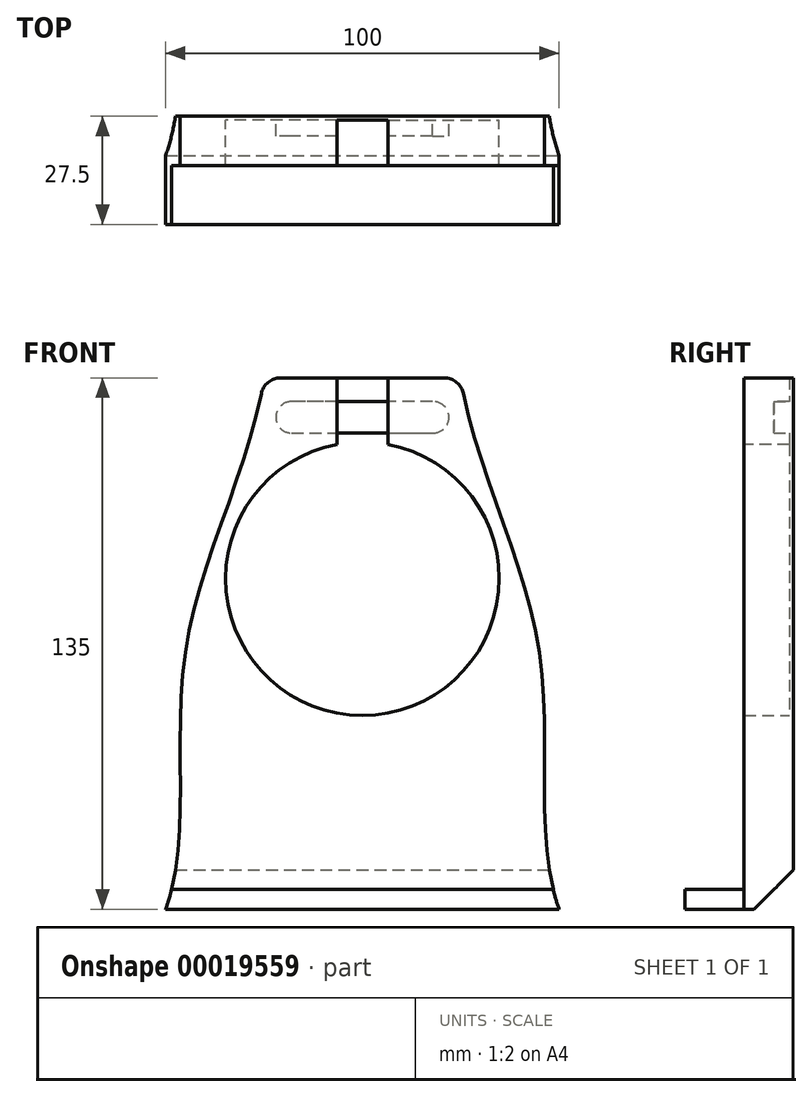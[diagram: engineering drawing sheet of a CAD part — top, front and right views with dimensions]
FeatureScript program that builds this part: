
annotation { "Feature Type Name" : "Feature", "Feature Type Description" : "" }
export const myFeature = defineFeature(function(context is Context, id is Id, definition is map)
    precondition{}
    {
        {
            var Q0;
            Q0=qCreatedBy(makeId("Front.planeOp"),FACE);
            var sketch = newSketch(context, id + "F0", { "sketchPlane" : qUnion([Q0])});
            skCircle(sketch, "E0", {"center": v(0, 84) * mm, "radius": 34.75 * mm});
            skLineSegment(sketch, "E1", {"start": v(-50, 0) * mm, "end": v(0, 0) * mm});
            skLineSegment(sketch, "E2", {"start": v(-20.79, 135) * mm, "end": v(0, 135) * mm});
            skFitSpline(sketch, "E3", {"points": [v(-50, 0) * mm, v(-45, 65.07) * mm, v(-24.94, 135) * mm], "startDerivative": vector(40.67, 111.81) * mm, "endDerivative": vector(23.97, 143.13) * mm});
            skLineSegment(sketch, "E4", {"start": v(0, 144.2) * mm, "end": v(0, -28.62) * mm, "construction": true});
            skLineSegment(sketch, "E5.MirrorCS", {"start": v(20.79, 135) * mm, "end": v(0, 135) * mm});
            skFitSpline(sketch, "E6.MirrorCS", {"points": [v(50, 0) * mm, v(45, 65.07) * mm, v(24.94, 135) * mm], "startDerivative": vector(-40.67, 111.81) * mm, "endDerivative": vector(-23.97, 143.13) * mm});
            skLineSegment(sketch, "E7.MirrorCS", {"start": v(50, 0) * mm, "end": v(0, 0) * mm});
            skArc(sketch, "E8.filletArc", {"start": v(-20.79, 135) * mm, "mid": v(-23.95, 133.87) * mm, "end": v(-25.69, 131) * mm});
            skArc(sketch, "E9.filletArc", {"start": v(25.69, 131) * mm, "mid": v(23.95, 133.87) * mm, "end": v(20.79, 135) * mm});
            skSolve(sketch);
        }
        {
            var Q0;
            Q0=makeQuery(id+"F0.imprint","IMPRINT",FACE,{"disambiguationData":[TD([[makeQuery(id+"F0.imprint","IMPRINT",EDGE,{"derivedFrom":sQuery(id+"F0.wireOp",EDGE,"E0")}),1.0]])]});
            extrude(context, id + "F1", {"entities" : qUnion([Q0]), "offsetDistance" : 25 * mm, "depth" : 1 * mm});
        }
        {
            var Q0;
            Q0 = qSketchRegion(id + "F0", true);
            extrude(context, id + "F2", {"entities" : qUnion([Q0]), "operationType" : NewBodyOperationType.ADD, "offsetDistance" : 25 * mm, "depth" : 12.5 * mm});
        }
        {
            var Q0;
            Q0=makeQuery(id+"F2.opExtrude","CAP_FACE",FACE,{"disambiguationData":[OSD([sQuery(id+"F0.wireOp",EDGE,"E0"),sQuery(id+"F0.wireOp",EDGE,"E1"),sQuery(id+"F0.wireOp",EDGE,"E2"),sQuery(id+"F0.wireOp",EDGE,"E3"),sQuery(id+"F0.wireOp",EDGE,"E5.MirrorCS"),sQuery(id+"F0.wireOp",EDGE,"E6.MirrorCS"),sQuery(id+"F0.wireOp",EDGE,"E7.MirrorCS"),sQuery(id+"F0.wireOp",EDGE,"E8.filletArc"),sQuery(id+"F0.wireOp",EDGE,"E9.filletArc")])],"isStart":false});
            var sketch = newSketch(context, id + "F3", { "sketchPlane" : qUnion([Q0])});
            skLineSegment(sketch, "E10", {"start": v(-48.5, 5) * mm, "end": v(48.5, 5) * mm});
            skLineSegment(sketch, "E11", {"start": v(-50, 0) * mm, "end": v(50, 0) * mm});
            skArc(sketch, "E12", {"start": v(-50, 0) * mm, "mid": v(-49.18, 2.48) * mm, "end": v(-48.5, 5) * mm});
            skArc(sketch, "E13", {"start": v(48.5, 5) * mm, "mid": v(49.17, 2.48) * mm, "end": v(50, 0) * mm});
            skSolve(sketch);
        }
        {
            var Q0;
            Q0 = qSketchRegion(id + "F3", true);
            extrude(context, id + "F4", {"entities" : qUnion([Q0]), "operationType" : NewBodyOperationType.ADD, "depth" : 15 * mm});
        }
        {
            var Q0;
            {var subQ0=sQuery(id+"F0.wireOp",EDGE,"E0");var subQ1=sQuery(id+"F0.wireOp",EDGE,"E2");var subQ2=sQuery(id+"F0.wireOp",EDGE,"E3");var subQ3=sQuery(id+"F0.wireOp",EDGE,"E5.MirrorCS");var subQ4=sQuery(id+"F0.wireOp",EDGE,"E6.MirrorCS");var subQ5=sQuery(id+"F0.wireOp",EDGE,"E8.filletArc");var subQ6=sQuery(id+"F0.wireOp",EDGE,"E9.filletArc");var subQ7=makeQuery(id+"F2.opExtrude","CAP_FACE",FACE,{"disambiguationData":[OSD([subQ0,sQuery(id+"F0.wireOp",EDGE,"E1"),subQ1,subQ2,subQ3,subQ4,sQuery(id+"F0.wireOp",EDGE,"E7.MirrorCS"),subQ5,subQ6])],"isStart":false});Q0=makeQuery(id+"F4.boolean.opBoolean","SPLIT",FACE,{"disambiguationData":[TD([makeQuery(id+"F2.opExtrude","SWEPT_FACE",FACE,{"disambiguationData":[OSD([subQ0])]})])],"derivedFrom":subQ7});}
            var sketch = newSketch(context, id + "F5", { "sketchPlane" : qUnion([Q0])});
            skLineSegment(sketch, "E14", {"start": v(-6.5, 135) * mm, "end": v(6.5, 135) * mm});
            skLineSegment(sketch, "E15", {"start": v(0, 114.05) * mm, "end": v(0, 95.22) * mm, "construction": true});
            skLineSegment(sketch, "E16", {"start": v(-6.5, 135) * mm, "end": v(-6.5, 118.14) * mm});
            skLineSegment(sketch, "E17", {"start": v(6.5, 135) * mm, "end": v(6.5, 118.14) * mm});
            skArc(sketch, "E18", {"start": v(6.5, 118.14) * mm, "mid": v(0, 118.75) * mm, "end": v(-6.5, 118.14) * mm});
            skSolve(sketch);
        }
        {
            var Q0;
            Q0 = qSketchRegion(id + "F5", true);
            extrude(context, id + "F6", {"entities" : qUnion([Q0]), "operationType" : NewBodyOperationType.REMOVE, "oppositeDirection" : true, "depth" : 11.5 * mm});
        }
        {
            var Q0;
            {var subQ0=sQuery(id+"F0.wireOp",EDGE,"E0");Q0=makeQuery(id+"F2.boolean.opBoolean","MERGE",FACE,{"derivedFrom":[makeQuery(id+"F1.opExtrude","CAP_FACE",FACE,{"disambiguationData":[OSD([subQ0])],"isStart":true}),makeQuery(id+"F2.opExtrude","CAP_FACE",FACE,{"disambiguationData":[OSD([subQ0,sQuery(id+"F0.wireOp",EDGE,"E1"),sQuery(id+"F0.wireOp",EDGE,"E2"),sQuery(id+"F0.wireOp",EDGE,"E3"),sQuery(id+"F0.wireOp",EDGE,"E5.MirrorCS"),sQuery(id+"F0.wireOp",EDGE,"E6.MirrorCS"),sQuery(id+"F0.wireOp",EDGE,"E7.MirrorCS"),sQuery(id+"F0.wireOp",EDGE,"E8.filletArc"),sQuery(id+"F0.wireOp",EDGE,"E9.filletArc")])],"isStart":true})]});}
            var sketch = newSketch(context, id + "F7", { "sketchPlane" : qUnion([Q0])});
            skArc(sketch, "E19", {"start": v(-17.77, 129) * mm, "mid": v(-22, 125) * mm, "end": v(-17.77, 121) * mm});
            skArc(sketch, "E20", {"start": v(18, 121) * mm, "mid": v(22, 125) * mm, "end": v(18, 129) * mm});
            skLineSegment(sketch, "E21", {"start": v(0, 111.96) * mm, "end": v(0, 95.55) * mm, "construction": true});
            skLineSegment(sketch, "E22", {"start": v(-18, 125) * mm, "end": v(18, 125) * mm, "construction": true});
            skLineSegment(sketch, "E23", {"start": v(-17.77, 129) * mm, "end": v(18, 129) * mm});
            skLineSegment(sketch, "E24", {"start": v(18, 121) * mm, "end": v(-17.77, 121) * mm});
            skSolve(sketch);
        }
        {
            var Q0;
            Q0 = qSketchRegion(id + "F7", true);
            extrude(context, id + "F8", {"entities" : qUnion([Q0]), "operationType" : NewBodyOperationType.REMOVE, "oppositeDirection" : true, "offsetDistance" : 25 * mm, "depth" : 5 * mm});
        }
        {
            var Q0;
            Q0=qCreatedBy(makeId("Right.planeOp"),FACE);
            var sketch = newSketch(context, id + "F9", { "sketchPlane" : qUnion([Q0])});
            skLineSegment(sketch, "E25", {"start": v(0, 0) * mm, "end": v(0, 10) * mm});
            skLineSegment(sketch, "E26", {"start": v(0, 10) * mm, "end": v(-10, 0) * mm});
            skLineSegment(sketch, "E27", {"start": v(-10, 0) * mm, "end": v(0, 0) * mm});
            skSolve(sketch);
        }
        {
            var Q0;
            Q0 = qSketchRegion(id + "F9", true);
            extrude(context, id + "F10", {"entities" : qUnion([Q0]), "operationType" : NewBodyOperationType.REMOVE, "endBound" : BoundingType.THROUGH_ALL, "oppositeDirection" : true, "depth" : 25 * mm, "offsetDistance" : 25 * mm, "hasSecondDirection" : true, "secondDirectionBound" : SecondDirectionBoundingType.THROUGH_ALL, "secondDirectionOppositeDirection" : false, "secondDirectionDepth" : 25 * mm});
        }
    });
